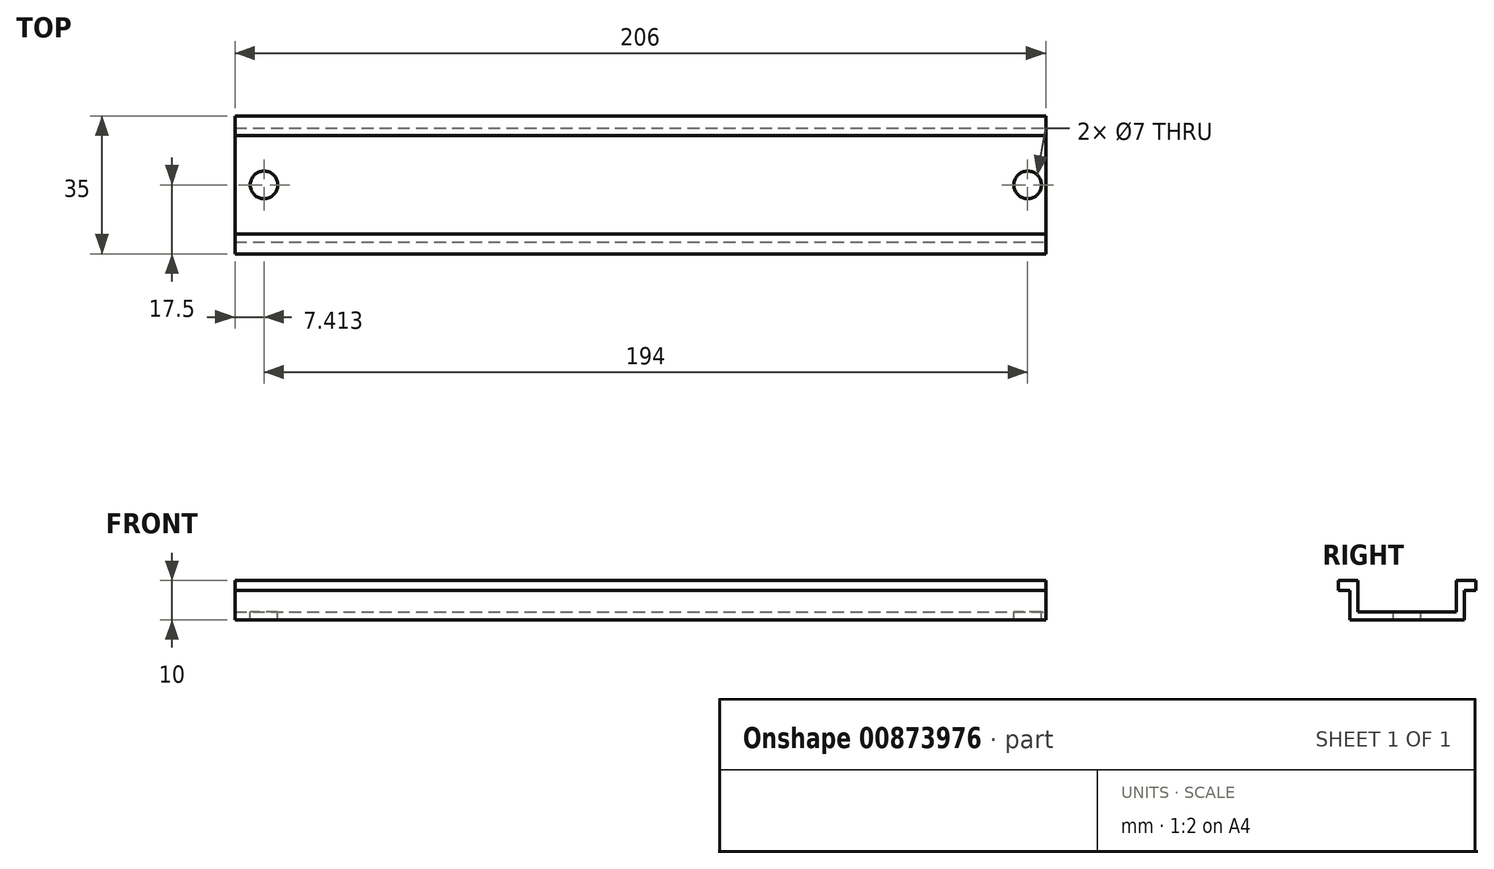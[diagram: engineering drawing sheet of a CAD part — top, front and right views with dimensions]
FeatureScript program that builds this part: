
annotation { "Feature Type Name" : "Feature", "Feature Type Description" : "" }
export const myFeature = defineFeature(function(context is Context, id is Id, definition is map)
    precondition{}
    {
        {
            var Q0;
            Q0=qCreatedBy(makeId("Top.planeOp"),FACE);
            var sketch = newSketch(context, id + "F0", { "sketchPlane" : qUnion([Q0])});
            skLineSegment(sketch, "E0.bottom", {"start": v(-103, 17.5) * mm, "end": v(103, 17.5) * mm});
            skLineSegment(sketch, "E0.top", {"start": v(-103, -17.5) * mm, "end": v(103, -17.5) * mm});
            skLineSegment(sketch, "E0.left", {"start": v(-103, 17.5) * mm, "end": v(-103, -17.5) * mm});
            skLineSegment(sketch, "E0.right", {"start": v(103, 17.5) * mm, "end": v(103, -17.5) * mm});
            skPoint(sketch, "E0.middle", {"position": v(0, 0) * mm});
            skPoint(sketch, "E1", {"position": v(-97, 0) * mm});
            skPoint(sketch, "E2.MirrorP", {"position": v(97, 0) * mm});
            skSolve(sketch);
        }
        {
            var Q0;
            Q0=makeQuery(id+"F0.imprint","IMPRINT",FACE,{"disambiguationData":[TD([[makeQuery(id+"F0.imprint","IMPRINT",EDGE,{"derivedFrom":sQuery(id+"F0.wireOp",EDGE,"E0.bottom")}),-1.0]])]});
            extrude(context, id + "F1", {"entities" : qUnion([Q0]), "depth" : 10 * mm, "offsetDistance" : 25 * mm});
        }
        {
            var Q0;
            Q0=makeQuery(id+"F1.opExtrude","SWEPT_FACE",FACE,{"disambiguationData":[OSD([sQuery(id+"F0.wireOp",EDGE,"E0.right")])]});
            var sketch = newSketch(context, id + "F2", { "sketchPlane" : qUnion([Q0])});
            skLineSegment(sketch, "E3.bottom", {"start": v(-12.5, 10) * mm, "end": v(12.5, 10) * mm});
            skLineSegment(sketch, "E3.top", {"start": v(-12.5, 2) * mm, "end": v(12.5, 2) * mm});
            skLineSegment(sketch, "E3.left", {"start": v(-12.5, 10) * mm, "end": v(-12.5, 2) * mm});
            skLineSegment(sketch, "E3.right", {"start": v(12.5, 10) * mm, "end": v(12.5, 2) * mm});
            skSolve(sketch);
        }
        {
            var Q0;
            Q0=makeQuery(id+"F2.imprint","IMPRINT",FACE,{"disambiguationData":[TD([[makeQuery(id+"F2.imprint","IMPRINT",EDGE,{"derivedFrom":sQuery(id+"F2.wireOp",EDGE,"E3.bottom")}),1.0]])]});
            extrude(context, id + "F3", {"entities" : qUnion([Q0]), "operationType" : NewBodyOperationType.REMOVE, "oppositeDirection" : true, "depth" : 25 * mm, "offsetDistance" : 25 * mm});
        }
        {
            var Q0;
            Q0=makeQuery(id+"F3.boolean.opBoolean","COPY",FACE,{"derivedFrom":makeQuery(id+"F3.opExtrude","CAP_FACE",FACE,{"disambiguationData":[OSD([sQuery(id+"F2.wireOp",EDGE,"E3.bottom"),sQuery(id+"F2.wireOp",EDGE,"E3.top"),sQuery(id+"F2.wireOp",EDGE,"E3.left"),sQuery(id+"F2.wireOp",EDGE,"E3.right")])],"isStart":false})});
            extrude(context, id + "F4", {"entities" : qUnion([Q0]), "operationType" : NewBodyOperationType.REMOVE, "endBound" : BoundingType.THROUGH_ALL, "oppositeDirection" : true, "depth" : 25 * mm, "offsetDistance" : 25 * mm});
        }
        {
            var Q0;
            Q0=makeQuery(id+"F1.opExtrude","SWEPT_FACE",FACE,{"disambiguationData":[OSD([sQuery(id+"F0.wireOp",EDGE,"E0.right")])]});
            var sketch = newSketch(context, id + "F5", { "sketchPlane" : qUnion([Q0])});
            skLineSegment(sketch, "E4.bottom", {"start": v(17.5, 7.5) * mm, "end": v(14.5, 7.5) * mm});
            skLineSegment(sketch, "E4.top", {"start": v(17.5, 0) * mm, "end": v(14.5, 0) * mm});
            skLineSegment(sketch, "E4.left", {"start": v(17.5, 7.5) * mm, "end": v(17.5, 0) * mm});
            skLineSegment(sketch, "E4.right", {"start": v(14.5, 7.5) * mm, "end": v(14.5, 0) * mm});
            skLineSegment(sketch, "E5.MirrorCS", {"start": v(-14.5, 7.5) * mm, "end": v(-14.5, 0) * mm});
            skLineSegment(sketch, "E6.MirrorCS", {"start": v(-17.5, 7.5) * mm, "end": v(-14.5, 7.5) * mm});
            skSolve(sketch);
        }
        {
            var Q0;
            Q0=makeQuery(id+"F5.imprint","IMPRINT",FACE,{"disambiguationData":[TD([[makeQuery(id+"F5.imprint","IMPRINT",EDGE,{"derivedFrom":sQuery(id+"F5.wireOp",EDGE,"E4.bottom")}),1.0]])]});
            var Q1;
            {var subQ0=sQuery(id+"F5.wireOp",EDGE,"E5.MirrorCS");Q1=makeQuery(id+"F5.imprint","IMPRINT",FACE,{"disambiguationData":[TD([[makeQuery(id+"F5.imprint","IMPRINT",EDGE,{"derivedFrom":subQ0}),-1.0]])]});}
            extrude(context, id + "F6", {"entities" : qUnion([Q0, Q1]), "operationType" : NewBodyOperationType.REMOVE, "endBound" : BoundingType.THROUGH_ALL, "oppositeDirection" : true, "depth" : 25 * mm, "offsetDistance" : 25 * mm});
        }
        {
            var Q0;
            {var subQ0=sQuery(id+"F2.wireOp",EDGE,"E3.top");Q0=makeQuery(id+"F4.boolean.opBoolean","MERGE",FACE,{"derivedFrom":[makeQuery(id+"F3.boolean.opBoolean","COPY",FACE,{"derivedFrom":makeQuery(id+"F3.opExtrude","SWEPT_FACE",FACE,{"disambiguationData":[OSD([subQ0])]})})],"fromTools":[makeQuery(id+"F4.opExtrude","SWEPT_FACE",FACE,{"disambiguationData":[OSD([subQ0])]})]});}
            var sketch = newSketch(context, id + "F7", { "sketchPlane" : qUnion([Q0])});
            skPoint(sketch, "E7", {"position": v(-95.59, 0) * mm});
            skPoint(sketch, "E8", {"position": v(98.41, 0) * mm});
            skSolve(sketch);
        }
        {
            var Q0;
            Q0=sQuery(id+"F7.wireOp",VERTEX,"E7");
            var Q1;
            Q1=sQuery(id+"F7.wireOp",VERTEX,"E8");
            var Q2;
            Q2=makeQuery(id+"F1.opExtrude","SWEPT_BODY",BODY,{"disambiguationData":[OSD([sQuery(id+"F0.wireOp",EDGE,"E0.bottom"),sQuery(id+"F0.wireOp",EDGE,"E0.top"),sQuery(id+"F0.wireOp",EDGE,"E0.left"),sQuery(id+"F0.wireOp",EDGE,"E0.right")])]});
            hole(context, id + "F8", {"style" : HoleStyle.SIMPLE, "endStyle" : HoleEndStyle.BLIND, "holeDiameter" : 7 * mm, "majorDiameter" : 5 * mm, "holeDepth" : 14.4 * mm, "isTappedThrough" : true, "tappedDepth" : 12 * mm, "tapClearance" : 3, "locations" : qUnion([Q0, Q1]), "scope" : qUnion([Q2])});
        }
    });
